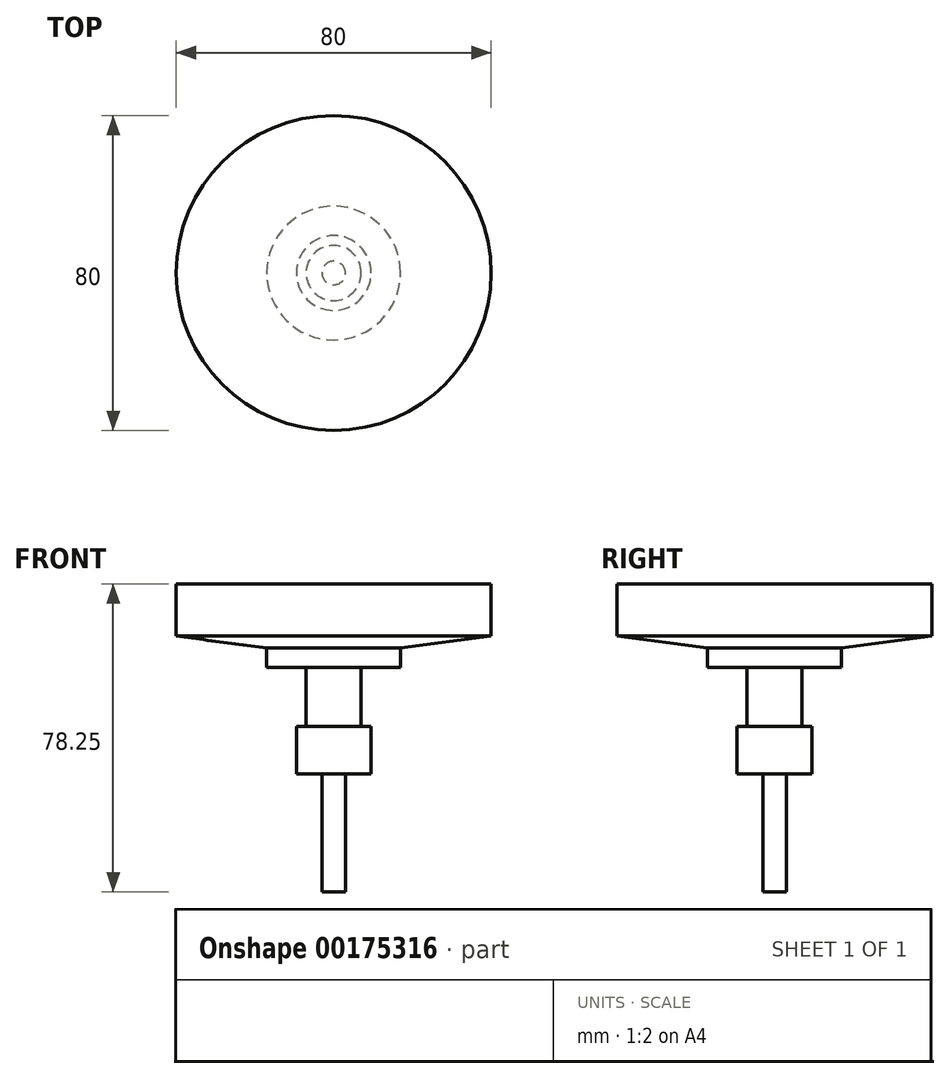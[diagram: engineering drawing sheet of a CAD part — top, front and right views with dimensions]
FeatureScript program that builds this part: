
annotation { "Feature Type Name" : "Feature", "Feature Type Description" : "" }
export const myFeature = defineFeature(function(context is Context, id is Id, definition is map)
    precondition{}
    {
        {
            var Q0;
            Q0=qCreatedBy(makeId("Front.planeOp"),FACE);
            var sketch = newSketch(context, id + "F0", { "sketchPlane" : qUnion([Q0])});
            skLineSegment(sketch, "E0", {"start": v(0, 0) * mm, "end": v(3, 0) * mm});
            skLineSegment(sketch, "E1", {"start": v(3, 0) * mm, "end": v(3, 30) * mm});
            skLineSegment(sketch, "E2", {"start": v(3, 30) * mm, "end": v(9.5, 30) * mm});
            skLineSegment(sketch, "E3", {"start": v(9.5, 30) * mm, "end": v(9.5, 42) * mm});
            skLineSegment(sketch, "E4", {"start": v(9.5, 42) * mm, "end": v(7, 42) * mm});
            skLineSegment(sketch, "E5", {"start": v(7, 42) * mm, "end": v(7, 57) * mm});
            skLineSegment(sketch, "E6", {"start": v(7, 57) * mm, "end": v(17, 57) * mm});
            skLineSegment(sketch, "E7", {"start": v(17, 57) * mm, "end": v(17, 62) * mm});
            skLineSegment(sketch, "E8", {"start": v(17, 62) * mm, "end": v(40, 65) * mm});
            skLineSegment(sketch, "E9", {"start": v(40, 65) * mm, "end": v(40, 78.25) * mm});
            skLineSegment(sketch, "E10", {"start": v(0, 0) * mm, "end": v(0, 78.25) * mm});
            skLineSegment(sketch, "E11", {"start": v(0, 78.25) * mm, "end": v(40, 78.25) * mm});
            skSolve(sketch);
        }
        {
            var Q0;
            Q0=makeQuery(id+"F0.imprint","IMPRINT",FACE,{"disambiguationData":[TD([[makeQuery(id+"F0.imprint","IMPRINT",EDGE,{"derivedFrom":sQuery(id+"F0.wireOp",EDGE,"E0")}),1.0]])]});
            var Q1;
            Q1=sQuery(id+"F0.wireOp",EDGE,"E10");
            revolve(context, id + "F1", {"entities" : qUnion([Q0]), "axis" : qUnion([Q1]), "revolveType" : RevolveType.FULL});
        }
    });
